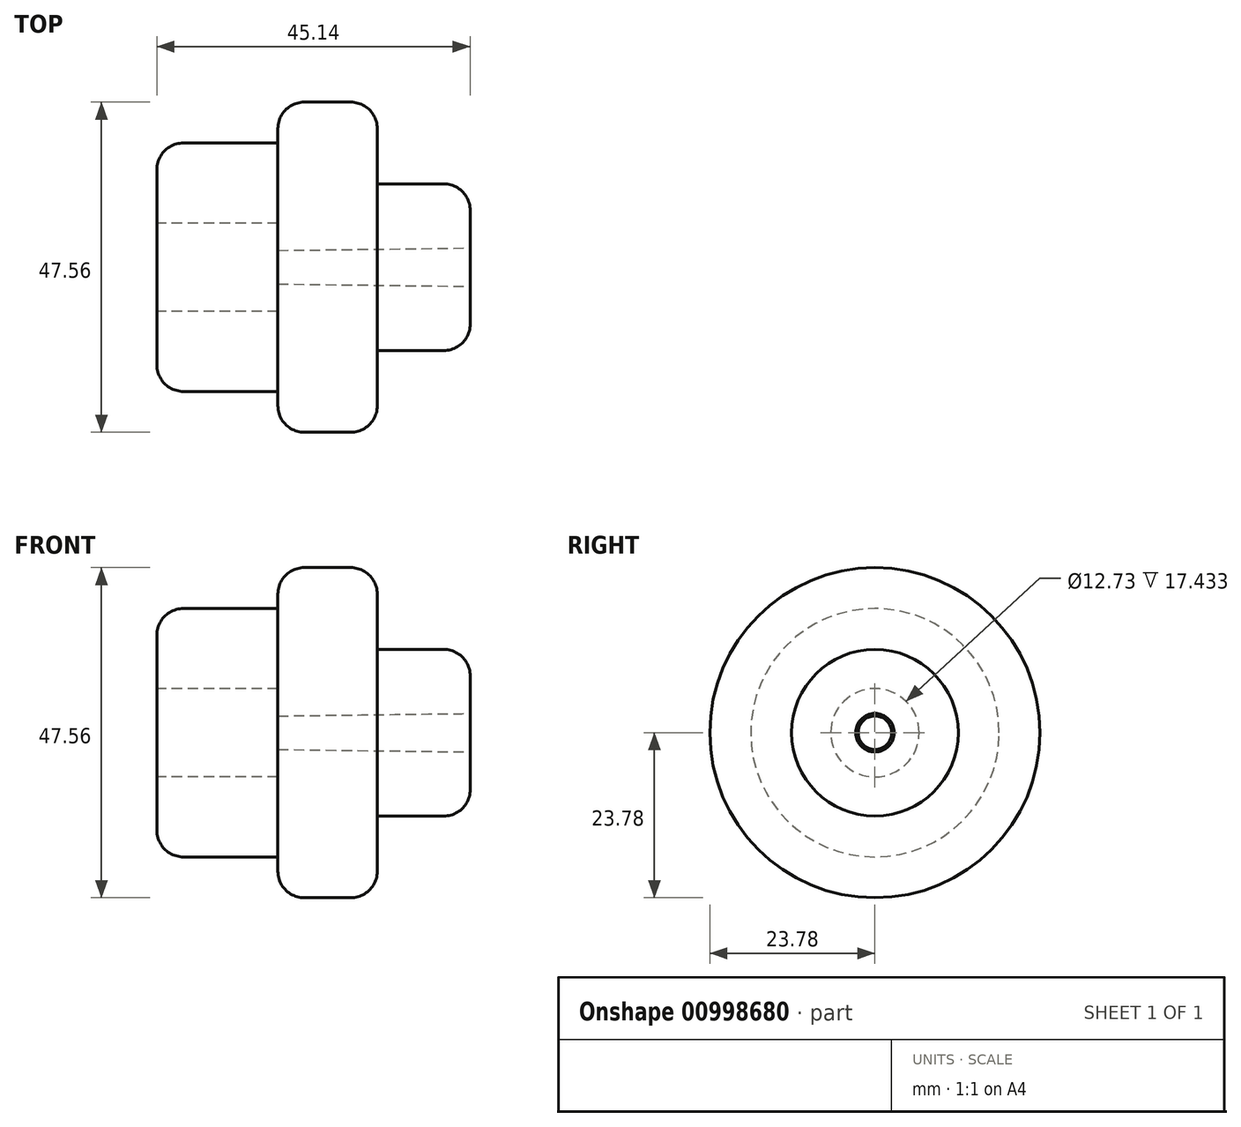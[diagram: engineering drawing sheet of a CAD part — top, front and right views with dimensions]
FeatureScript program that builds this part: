
annotation { "Feature Type Name" : "Feature", "Feature Type Description" : "" }
export const myFeature = defineFeature(function(context is Context, id is Id, definition is map)
    precondition{}
    {
        {
            var Q0;
            Q0=qCreatedBy(makeId("Front.planeOp"),FACE);
            var sketch = newSketch(context, id + "F0", { "sketchPlane" : qUnion([Q0])});
            skLineSegment(sketch, "E0", {"start": v(-75.97, 0) * mm, "end": v(75.97, 0) * mm, "construction": true});
            skLineSegment(sketch, "E1", {"start": v(33.71, 2.77) * mm, "end": v(33.71, 8.2) * mm});
            skLineSegment(sketch, "E2", {"start": v(29.9, 12) * mm, "end": v(20.32, 12) * mm});
            skLineSegment(sketch, "E3", {"start": v(20.32, 12) * mm, "end": v(20.32, 19.97) * mm});
            skLineSegment(sketch, "E4", {"start": v(16.51, 23.78) * mm, "end": v(9.81, 23.78) * mm});
            skLineSegment(sketch, "E5", {"start": v(6, 19.97) * mm, "end": v(6, 12) * mm});
            skLineSegment(sketch, "E6", {"start": v(6, 12) * mm, "end": v(6, 2.41) * mm});
            skLineSegment(sketch, "E7", {"start": v(-11.43, 14.09) * mm, "end": v(-11.43, 6.36) * mm});
            skPoint(sketch, "E7.startSnap0", {"position": v(6, 17.9) * mm});
            skLineSegment(sketch, "E8", {"start": v(-11.43, 6.36) * mm, "end": v(6, 6.36) * mm});
            skLineSegment(sketch, "E9", {"start": v(-7.62, 17.9) * mm, "end": v(6, 17.9) * mm});
            skPoint(sketch, "E10.visualSharp", {"position": v(33.71, 12) * mm});
            skArc(sketch, "E10.filletArc", {"start": v(33.71, 8.2) * mm, "mid": v(32.6, 10.9) * mm, "end": v(29.9, 12) * mm});
            skPoint(sketch, "E11.visualSharp", {"position": v(20.32, 23.78) * mm});
            skArc(sketch, "E11.filletArc", {"start": v(20.32, 19.97) * mm, "mid": v(19.2, 22.67) * mm, "end": v(16.51, 23.78) * mm});
            skPoint(sketch, "E12.visualSharp", {"position": v(6, 23.78) * mm});
            skArc(sketch, "E12.filletArc", {"start": v(9.81, 23.78) * mm, "mid": v(7.12, 22.67) * mm, "end": v(6, 19.97) * mm});
            skPoint(sketch, "E13.visualSharp", {"position": v(-11.43, 17.9) * mm});
            skArc(sketch, "E13.filletArc", {"start": v(-7.62, 17.9) * mm, "mid": v(-10.31, 16.78) * mm, "end": v(-11.43, 14.09) * mm});
            skLineSegment(sketch, "E14", {"start": v(6, 2.41) * mm, "end": v(33.71, 2.77) * mm});
            skSolve(sketch);
        }
        {
            var Q0;
            Q0 = qSketchRegion(id + "F0", true);
            var Q1;
            Q1=sQuery(id+"F0.wireOp",EDGE,"E0");
            revolve(context, id + "F1", {"surfaceOperationType" : NewSurfaceOperationType.NEW, "entities" : qUnion([Q0]), "axis" : qUnion([Q1]), "revolveType" : RevolveType.FULL});
        }
    });
